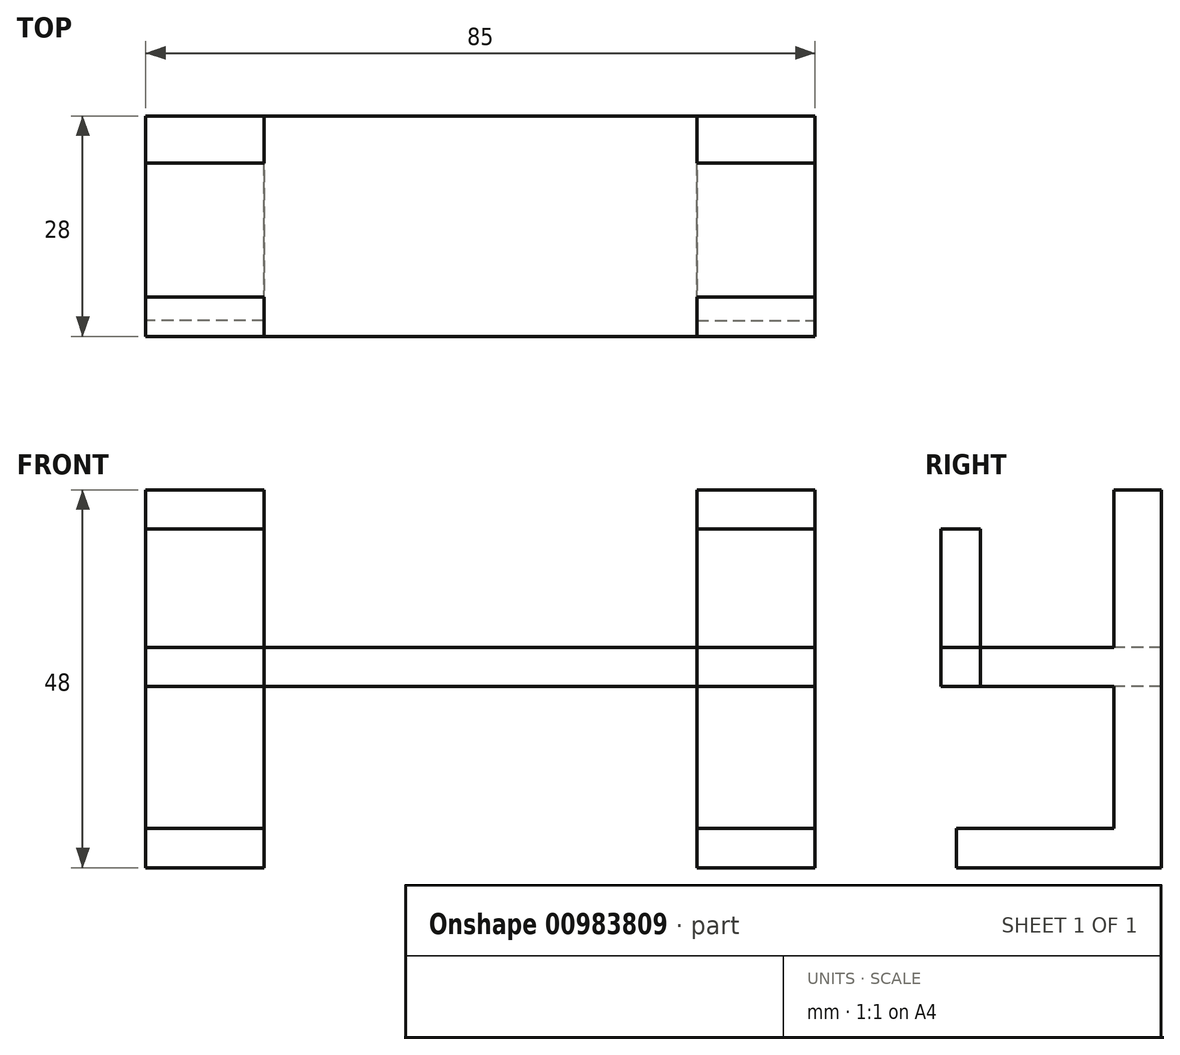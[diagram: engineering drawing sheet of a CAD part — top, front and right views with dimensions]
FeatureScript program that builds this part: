
annotation { "Feature Type Name" : "Feature", "Feature Type Description" : "" }
export const myFeature = defineFeature(function(context is Context, id is Id, definition is map)
    precondition{}
    {
        {
            var Q0;
            Q0=qCreatedBy(makeId("Top.planeOp"),FACE);
            var sketch = newSketch(context, id + "F0", { "sketchPlane" : qUnion([Q0])});
            skLineSegment(sketch, "E0.bottom", {"start": v(-42.5, 0) * mm, "end": v(42.5, 0) * mm});
            skLineSegment(sketch, "E0.top", {"start": v(-42.5, -28) * mm, "end": v(42.5, -28) * mm});
            skLineSegment(sketch, "E0.left", {"start": v(-42.5, 0) * mm, "end": v(-42.5, -28) * mm});
            skLineSegment(sketch, "E0.right", {"start": v(42.5, 0) * mm, "end": v(42.5, -28) * mm});
            skLineSegment(sketch, "E1", {"start": v(-42.5, -6) * mm, "end": v(42.5, -6) * mm});
            skLineSegment(sketch, "E2", {"start": v(-42.5, -23) * mm, "end": v(42.5, -23) * mm});
            skLineSegment(sketch, "E3", {"start": v(27.5, 0) * mm, "end": v(27.5, -28) * mm});
            skLineSegment(sketch, "E4", {"start": v(-27.5, 0) * mm, "end": v(-27.5, -28) * mm});
            skSolve(sketch);
        }
        {
            var Q0;
            {var subQ0=sQuery(id+"F0.wireOp",EDGE,"E0.left");var subQ1=sQuery(id+"F0.wireOp",EDGE,"E0.top");var subQ2=makeQuery(id+"F0.imprint","INTERSECT",VERTEX,{"derivedFrom":[subQ1,subQ0]});Q0=makeQuery(id+"F0.imprint","IMPRINT",FACE,{"disambiguationData":[TD([[makeQuery(id+"F0.imprint","IMPRINT",EDGE,{"disambiguationData":[TD([[subQ2,-1.0]])],"derivedFrom":subQ1}),1.0]])]});}
            var Q1;
            {var subQ0=sQuery(id+"F0.wireOp",EDGE,"E3");var subQ1=sQuery(id+"F0.wireOp",EDGE,"E0.top");var subQ2=makeQuery(id+"F0.imprint","INTERSECT",VERTEX,{"derivedFrom":[subQ1,subQ0]});Q1=makeQuery(id+"F0.imprint","IMPRINT",FACE,{"disambiguationData":[TD([[makeQuery(id+"F0.imprint","IMPRINT",EDGE,{"disambiguationData":[TD([[subQ2,1.0]])],"derivedFrom":subQ1}),1.0]])]});}
            var Q2;
            {var subQ0=sQuery(id+"F0.wireOp",EDGE,"E0.right");var subQ1=sQuery(id+"F0.wireOp",EDGE,"E0.top");var subQ2=makeQuery(id+"F0.imprint","INTERSECT",VERTEX,{"derivedFrom":[subQ1,subQ0]});Q2=makeQuery(id+"F0.imprint","IMPRINT",FACE,{"disambiguationData":[TD([[makeQuery(id+"F0.imprint","IMPRINT",EDGE,{"disambiguationData":[TD([[subQ2,1.0]])],"derivedFrom":subQ1}),1.0]])]});}
            var Q3;
            {var subQ0=sQuery(id+"F0.wireOp",EDGE,"E0.right");var subQ1=sQuery(id+"F0.wireOp",EDGE,"E0.bottom");var subQ2=makeQuery(id+"F0.imprint","INTERSECT",VERTEX,{"derivedFrom":[subQ1,subQ0]});Q3=makeQuery(id+"F0.imprint","IMPRINT",FACE,{"disambiguationData":[TD([[makeQuery(id+"F0.imprint","IMPRINT",EDGE,{"disambiguationData":[TD([[subQ2,1.0]])],"derivedFrom":subQ1}),-1.0]])]});}
            var Q4;
            {var subQ0=sQuery(id+"F0.wireOp",EDGE,"E3");var subQ1=sQuery(id+"F0.wireOp",EDGE,"E0.bottom");var subQ2=makeQuery(id+"F0.imprint","INTERSECT",VERTEX,{"derivedFrom":[subQ1,subQ0]});Q4=makeQuery(id+"F0.imprint","IMPRINT",FACE,{"disambiguationData":[TD([[makeQuery(id+"F0.imprint","IMPRINT",EDGE,{"disambiguationData":[TD([[subQ2,1.0]])],"derivedFrom":subQ1}),-1.0]])]});}
            var Q5;
            {var subQ0=sQuery(id+"F0.wireOp",EDGE,"E0.left");var subQ1=sQuery(id+"F0.wireOp",EDGE,"E0.bottom");var subQ2=makeQuery(id+"F0.imprint","INTERSECT",VERTEX,{"derivedFrom":[subQ1,subQ0]});Q5=makeQuery(id+"F0.imprint","IMPRINT",FACE,{"disambiguationData":[TD([[makeQuery(id+"F0.imprint","IMPRINT",EDGE,{"disambiguationData":[TD([[subQ2,-1.0]])],"derivedFrom":subQ1}),-1.0]])]});}
            var Q6;
            {var subQ0=sQuery(id+"F0.wireOp",EDGE,"E1");var subQ1=sQuery(id+"F0.wireOp",EDGE,"E0.left");var subQ2=makeQuery(id+"F0.imprint","INTERSECT",VERTEX,{"derivedFrom":[subQ1,subQ0]});Q6=makeQuery(id+"F0.imprint","IMPRINT",FACE,{"disambiguationData":[TD([[makeQuery(id+"F0.imprint","IMPRINT",EDGE,{"disambiguationData":[TD([[subQ2,-1.0]])],"derivedFrom":subQ1}),1.0]])]});}
            var Q7;
            {var subQ0=sQuery(id+"F0.wireOp",EDGE,"E4");var subQ1=sQuery(id+"F0.wireOp",EDGE,"E1");var subQ2=makeQuery(id+"F0.imprint","INTERSECT",VERTEX,{"derivedFrom":[subQ1,subQ0]});Q7=makeQuery(id+"F0.imprint","IMPRINT",FACE,{"disambiguationData":[TD([[makeQuery(id+"F0.imprint","IMPRINT",EDGE,{"disambiguationData":[TD([[subQ2,-1.0]])],"derivedFrom":subQ1}),-1.0]])]});}
            var Q8;
            {var subQ0=sQuery(id+"F0.wireOp",EDGE,"E1");var subQ1=sQuery(id+"F0.wireOp",EDGE,"E0.right");var subQ2=makeQuery(id+"F0.imprint","INTERSECT",VERTEX,{"derivedFrom":[subQ1,subQ0]});Q8=makeQuery(id+"F0.imprint","IMPRINT",FACE,{"disambiguationData":[TD([[makeQuery(id+"F0.imprint","IMPRINT",EDGE,{"disambiguationData":[TD([[subQ2,-1.0]])],"derivedFrom":subQ1}),-1.0]])]});}
            extrude(context, id + "F1", {"entities" : qUnion([Q0, Q1, Q2, Q3, Q4, Q5, Q6, Q7, Q8]), "depth" : 5 * mm, "offsetDistance" : 25 * mm});
        }
        {
            var Q0;
            {var subQ0=sQuery(id+"F0.wireOp",EDGE,"E0.left");var subQ1=sQuery(id+"F0.wireOp",EDGE,"E0.top");var subQ2=makeQuery(id+"F0.imprint","INTERSECT",VERTEX,{"derivedFrom":[subQ1,subQ0]});Q0=makeQuery(id+"F0.imprint","IMPRINT",FACE,{"disambiguationData":[TD([[makeQuery(id+"F0.imprint","IMPRINT",EDGE,{"disambiguationData":[TD([[subQ2,-1.0]])],"derivedFrom":subQ1}),1.0]])]});}
            var Q1;
            {var subQ0=sQuery(id+"F0.wireOp",EDGE,"E0.right");var subQ1=sQuery(id+"F0.wireOp",EDGE,"E0.top");var subQ2=makeQuery(id+"F0.imprint","INTERSECT",VERTEX,{"derivedFrom":[subQ1,subQ0]});Q1=makeQuery(id+"F0.imprint","IMPRINT",FACE,{"disambiguationData":[TD([[makeQuery(id+"F0.imprint","IMPRINT",EDGE,{"disambiguationData":[TD([[subQ2,1.0]])],"derivedFrom":subQ1}),1.0]])]});}
            extrude(context, id + "F2", {"entities" : qUnion([Q0, Q1]), "depth" : 20 * mm, "offsetDistance" : 25 * mm});
        }
        {
            var Q0;
            {var subQ0=sQuery(id+"F0.wireOp",EDGE,"E0.left");var subQ1=sQuery(id+"F0.wireOp",EDGE,"E0.bottom");var subQ2=makeQuery(id+"F0.imprint","INTERSECT",VERTEX,{"derivedFrom":[subQ1,subQ0]});Q0=makeQuery(id+"F0.imprint","IMPRINT",FACE,{"disambiguationData":[TD([[makeQuery(id+"F0.imprint","IMPRINT",EDGE,{"disambiguationData":[TD([[subQ2,-1.0]])],"derivedFrom":subQ1}),-1.0]])]});}
            var Q1;
            {var subQ0=sQuery(id+"F0.wireOp",EDGE,"E0.right");var subQ1=sQuery(id+"F0.wireOp",EDGE,"E0.bottom");var subQ2=makeQuery(id+"F0.imprint","INTERSECT",VERTEX,{"derivedFrom":[subQ1,subQ0]});Q1=makeQuery(id+"F0.imprint","IMPRINT",FACE,{"disambiguationData":[TD([[makeQuery(id+"F0.imprint","IMPRINT",EDGE,{"disambiguationData":[TD([[subQ2,1.0]])],"derivedFrom":subQ1}),-1.0]])]});}
            extrude(context, id + "F3", {"entities" : qUnion([Q0, Q1]), "operationType" : NewBodyOperationType.ADD, "oppositeDirection" : true, "depth" : 23 * mm, "offsetDistance" : 25 * mm, "hasSecondDirection" : true, "secondDirectionOppositeDirection" : false, "secondDirectionDepth" : 25 * mm});
        }
        {
            var Q0;
            {var subQ0=sQuery(id+"F0.wireOp",EDGE,"E0.right");var subQ2=sQuery(id+"F0.wireOp",EDGE,"E1");var subQ3=sQuery(id+"F0.wireOp",EDGE,"E0.bottom");Q0=makeQuery(id+"F3.boolean.opBoolean","SPLIT",FACE,{"disambiguationData":[TD([makeQuery(id+"F1.opExtrude","CAP_FACE",FACE,{"disambiguationData":[OSD([subQ3,sQuery(id+"F0.wireOp",EDGE,"E0.top"),sQuery(id+"F0.wireOp",EDGE,"E0.left"),subQ0])],"isStart":true})])],"derivedFrom":makeQuery(id+"F3.opExtrude","SWEPT_FACE",FACE,{"disambiguationData":[OSD([subQ2]),TDD([makeQuery(id+"F0.imprint","IMPRINT",EDGE,{"disambiguationData":[TD([[makeQuery(id+"F0.imprint","INTERSECT",VERTEX,{"derivedFrom":[subQ0,subQ2]}),1.0]])],"derivedFrom":subQ2})])]})});}
            var sketch = newSketch(context, id + "F4", { "sketchPlane" : qUnion([Q0])});
            skPoint(sketch, "E5.oppositeSnap0", {"position": v(27.5, -11.5) * mm});
            skLineSegment(sketch, "E5.bottom", {"start": v(42.5, -23) * mm, "end": v(-42.5, -23) * mm});
            skLineSegment(sketch, "E5.top", {"start": v(42.5, -18) * mm, "end": v(-42.5, -18) * mm});
            skLineSegment(sketch, "E5.left", {"start": v(42.5, -23) * mm, "end": v(42.5, -18) * mm});
            skLineSegment(sketch, "E5.right", {"start": v(-42.5, -23) * mm, "end": v(-42.5, -18) * mm});
            skLineSegment(sketch, "E6", {"start": v(-27.5, -23) * mm, "end": v(-27.5, -18) * mm});
            skLineSegment(sketch, "E7", {"start": v(27.5, -23) * mm, "end": v(27.5, -11.5) * mm});
            skSolve(sketch);
        }
        {
            var Q0;
            {var subQ0=sQuery(id+"F4.wireOp",EDGE,"E5.left");Q0=makeQuery(id+"F4.imprint","IMPRINT",FACE,{"disambiguationData":[TD([[makeQuery(id+"F4.imprint","IMPRINT",EDGE,{"derivedFrom":subQ0}),1.0]])]});}
            var Q1;
            {var subQ0=sQuery(id+"F4.wireOp",EDGE,"E5.right");Q1=makeQuery(id+"F4.imprint","IMPRINT",FACE,{"disambiguationData":[TD([[makeQuery(id+"F4.imprint","IMPRINT",EDGE,{"derivedFrom":subQ0}),-1.0]])]});}
            extrude(context, id + "F5", {"entities" : qUnion([Q0, Q1]), "operationType" : NewBodyOperationType.ADD, "depth" : 20 * mm, "offsetDistance" : 25 * mm});
        }
    });
